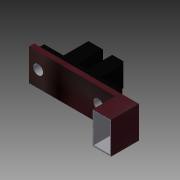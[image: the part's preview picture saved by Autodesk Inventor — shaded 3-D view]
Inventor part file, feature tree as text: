
AUTODESK INVENTOR PART (.ipt)
format: ipt  version: 2015 SP1 (Build 190203100, 203)  size: 162,816 bytes
history: native  units: mm
features: extrude x5, sketch x5
ambient origin geometry x8: Origin, YZ Plane, XZ Plane, XY Plane, X Axis, Y Axis, Z Axis, Center Point
bodies: Solid1 (feature_tree)
feature tree (10):
  extrude  "Extrusion1"  Depth=3.11mm
  extrude  "Extrusion2"  Depth=2.96mm
  extrude  "Extrusion3"  Depth=6.62mm
  extrude  "Extrusion4"  Depth=6.43mm TaperAngle=0.0deg
  extrude  "Extrusion5"  Depth=1.6mm
  sketch  "Sketch1"  dims[d0=24.6mm d1=3.11mm]
  sketch  "Sketch2"  dims[d2=4.39mm d3=2.96mm]
  sketch  "Sketch3"  dims[d4=4.52mm d5=6.62mm]
  sketch  "Sketch4"  dims[d6=7.84mm d7=6.43mm d8=0.0mm]
  sketch  "Sketch5"  dims[d9=1.76mm d10=1.6mm d11=1.3mm d12=1.3mm d13=6.43mm d14=0.0mm d15=32.89mm d16=10.0mm d17=1.6mm d18=0.0mm d19=5.78mm d20=7.17mm d21=0.0mm d22=7.33mm d23=0.0mm]
